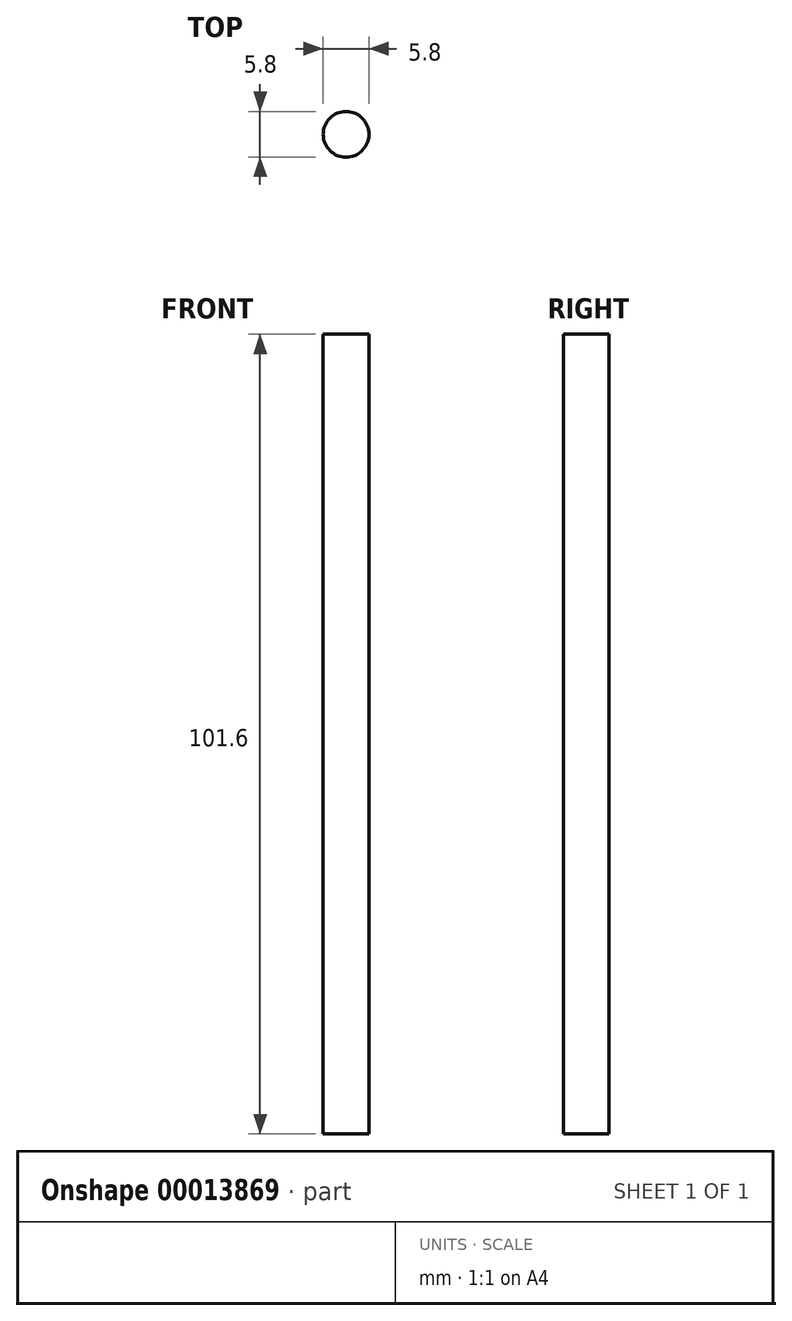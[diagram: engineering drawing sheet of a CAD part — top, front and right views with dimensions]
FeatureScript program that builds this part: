
annotation { "Feature Type Name" : "Feature", "Feature Type Description" : "" }
export const myFeature = defineFeature(function(context is Context, id is Id, definition is map)
    precondition{}
    {
        {
            var Q0;
            Q0=qCreatedBy(makeId("Top.planeOp"),FACE);
            var sketch = newSketch(context, id + "F0", { "sketchPlane" : qUnion([Q0])});
            skCircle(sketch, "E0", {"center": v(0, 0) * mm, "radius": 2.9 * mm});
            skSolve(sketch);
        }
        {
            var Q0;
            Q0 = qSketchRegion(id + "F0", true);
            extrude(context, id + "F1", {"entities" : qUnion([Q0]), "depth" : 101.6 * mm});
        }
    });
